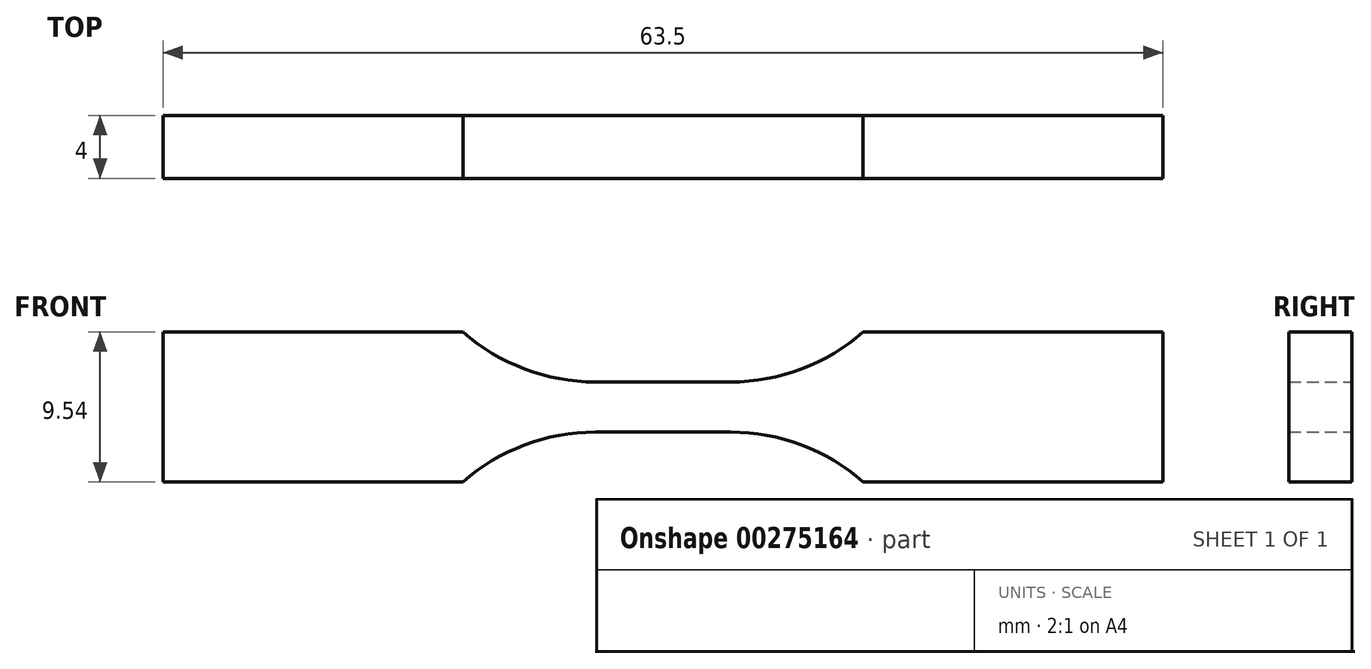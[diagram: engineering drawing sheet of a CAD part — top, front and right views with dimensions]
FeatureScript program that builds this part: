
annotation { "Feature Type Name" : "Feature", "Feature Type Description" : "" }
export const myFeature = defineFeature(function(context is Context, id is Id, definition is map)
    precondition{}
    {
        {
            var Q0;
            Q0=qCreatedBy(makeId("Front.planeOp"),FACE);
            var sketch = newSketch(context, id + "F0", { "sketchPlane" : qUnion([Q0])});
            skLineSegment(sketch, "E0", {"start": v(0, 1.59) * mm, "end": v(4.3, 1.59) * mm});
            skArc(sketch, "E1", {"start": v(4.3, 1.6) * mm, "mid": v(8.79, 2.41) * mm, "end": v(12.7, 4.77) * mm});
            skLineSegment(sketch, "E2", {"start": v(12.7, 4.77) * mm, "end": v(31.75, 4.77) * mm});
            skLineSegment(sketch, "E3", {"start": v(31.75, 4.76) * mm, "end": v(31.75, 0) * mm});
            skLineSegment(sketch, "E4.MirrorCS", {"start": v(0, -1.6) * mm, "end": v(4.3, -1.6) * mm});
            skLineSegment(sketch, "E5.MirrorCS", {"start": v(31.75, -4.76) * mm, "end": v(31.75, 0) * mm});
            skLineSegment(sketch, "E6.MirrorCS", {"start": v(12.7, -4.77) * mm, "end": v(31.75, -4.77) * mm});
            skArc(sketch, "E7.MirrorCS", {"start": v(4.3, -1.6) * mm, "mid": v(8.79, -2.41) * mm, "end": v(12.7, -4.77) * mm});
            skArc(sketch, "E8.MirrorCS", {"start": v(-4.3, -1.6) * mm, "mid": v(-8.79, -2.41) * mm, "end": v(-12.7, -4.77) * mm});
            skLineSegment(sketch, "E9.MirrorCS", {"start": v(-12.7, -4.77) * mm, "end": v(-31.75, -4.77) * mm});
            skArc(sketch, "E10.MirrorCS", {"start": v(-4.3, 1.6) * mm, "mid": v(-8.79, 2.41) * mm, "end": v(-12.7, 4.77) * mm});
            skLineSegment(sketch, "E11.MirrorCS", {"start": v(-12.7, 4.77) * mm, "end": v(-31.75, 4.76) * mm});
            skLineSegment(sketch, "E12.MirrorCS", {"start": v(-31.75, -4.76) * mm, "end": v(-31.75, 0) * mm});
            skLineSegment(sketch, "E13.MirrorCS", {"start": v(0, -1.59) * mm, "end": v(-4.3, -1.59) * mm});
            skLineSegment(sketch, "E14.MirrorCS", {"start": v(-31.75, 4.76) * mm, "end": v(-31.75, 0) * mm});
            skLineSegment(sketch, "E15.MirrorCS", {"start": v(0, 1.6) * mm, "end": v(-4.3, 1.6) * mm});
            skSolve(sketch);
        }
        {
            var Q0;
            Q0 = qSketchRegion(id + "F0", true);
            extrude(context, id + "F1", {"entities" : qUnion([Q0]), "endBound" : BoundingType.SYMMETRIC, "depth" : 4 * mm});
        }
    });
